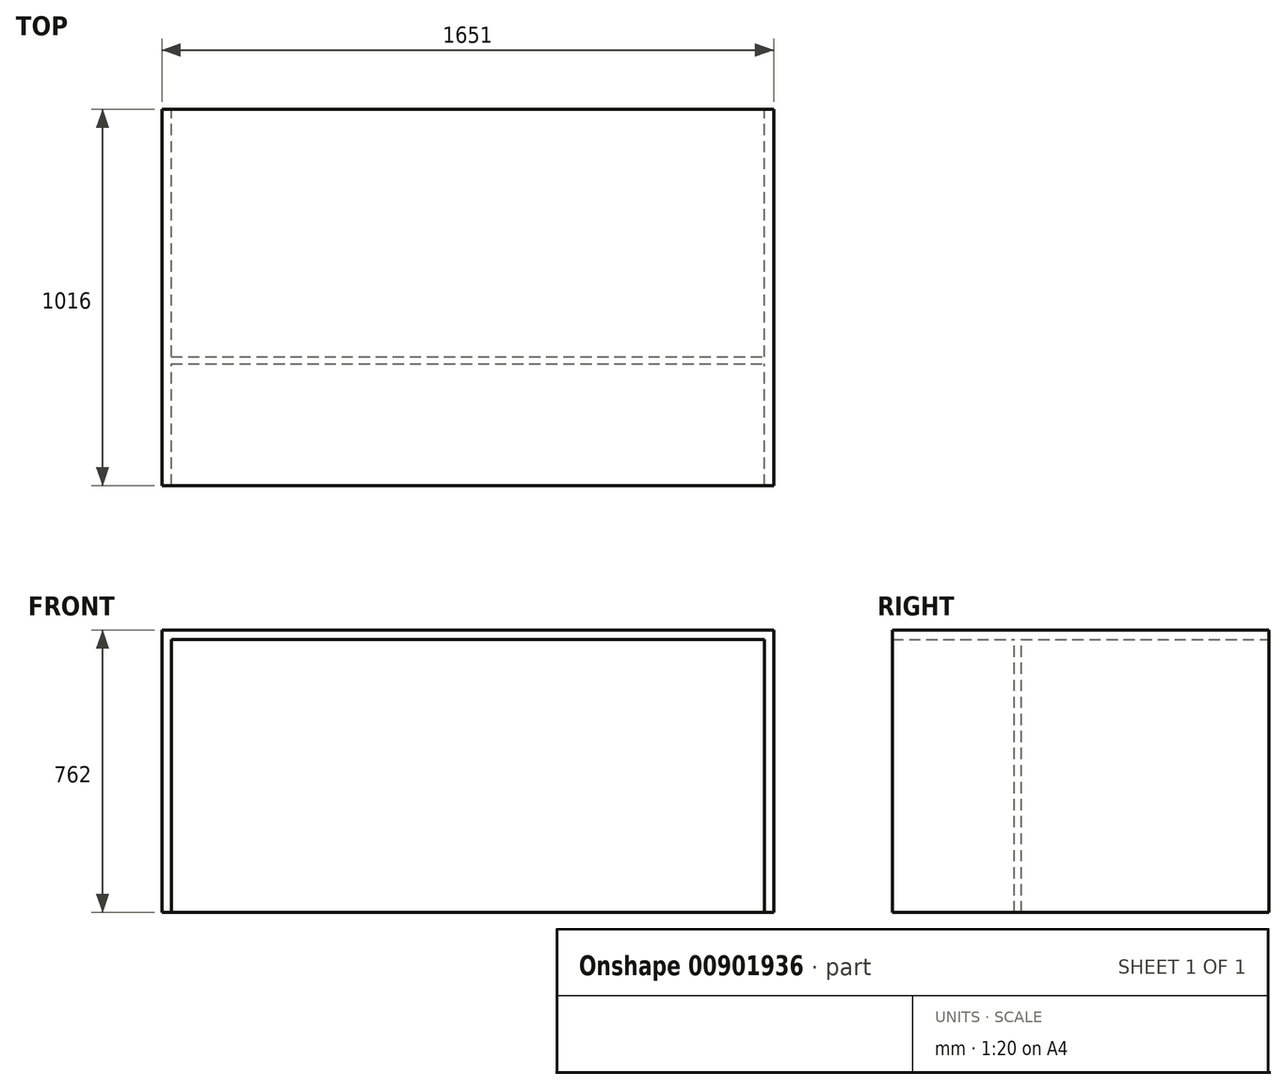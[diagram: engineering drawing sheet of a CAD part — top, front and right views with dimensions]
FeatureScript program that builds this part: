
annotation { "Feature Type Name" : "Feature", "Feature Type Description" : "" }
export const myFeature = defineFeature(function(context is Context, id is Id, definition is map)
    precondition{}
    {
        {
            assignVariable(context, id + "F0", {"name" : "height", "anyValue" : 762 * mm});
        }
        {
            assignVariable(context, id + "F1", {"name" : "width", "anyValue" : 1016 * mm});
        }
        {
            var Q0;
            Q0=qCreatedBy(makeId("Front.planeOp"),FACE);
            var sketch = newSketch(context, id + "F2", { "sketchPlane" : qUnion([Q0])});
            skLineSegment(sketch, "E0", {"start": v(0, 0) * mm, "end": v(25.4, 0) * mm});
            skLineSegment(sketch, "E1", {"start": v(25.4, 0) * mm, "end": v(25.4, 736.6) * mm});
            skLineSegment(sketch, "E2", {"start": v(25.4, 736.6) * mm, "end": v(0, 762) * mm});
            skLineSegment(sketch, "E3", {"start": v(0, 762) * mm, "end": v(0, 0) * mm});
            skLineSegment(sketch, "E4", {"start": v(0, 762) * mm, "end": v(1651, 762) * mm});
            skLineSegment(sketch, "E5", {"start": v(1651, 762) * mm, "end": v(1625.6, 736.6) * mm});
            skLineSegment(sketch, "E6", {"start": v(1625.6, 736.6) * mm, "end": v(25.4, 736.6) * mm});
            skLineSegment(sketch, "E7", {"start": v(1625.6, 736.6) * mm, "end": v(1625.6, 0) * mm});
            skLineSegment(sketch, "E8", {"start": v(1625.6, 0) * mm, "end": v(1651, 0) * mm});
            skLineSegment(sketch, "E9", {"start": v(1651, 0) * mm, "end": v(1651, 762) * mm});
            skSolve(sketch);
        }
        {
            var Q0;
            Q0=makeQuery(id+"F2.imprint","IMPRINT",FACE,{"disambiguationData":[TD([[makeQuery(id+"F2.imprint","IMPRINT",EDGE,{"derivedFrom":sQuery(id+"F2.wireOp",EDGE,"E0")}),1.0]])]});
            var Q1;
            Q1=makeQuery(id+"F2.imprint","IMPRINT",FACE,{"disambiguationData":[TD([[makeQuery(id+"F2.imprint","IMPRINT",EDGE,{"derivedFrom":sQuery(id+"F2.wireOp",EDGE,"E2")}),-1.0]])]});
            var Q2;
            Q2=makeQuery(id+"F2.imprint","IMPRINT",FACE,{"disambiguationData":[TD([[makeQuery(id+"F2.imprint","IMPRINT",EDGE,{"derivedFrom":sQuery(id+"F2.wireOp",EDGE,"E5")}),1.0]])]});
            extrude(context, id + "F3", {"entities" : qUnion([Q0, Q1, Q2]), "depth" : getVariable(context, 'width'), "offsetDistance" : 25.4 * mm});
        }
        {
            var Q0;
            Q0=makeQuery(id+"F3.opExtrude","SWEPT_FACE",FACE,{"disambiguationData":[OSD([sQuery(id+"F2.wireOp",EDGE,"E6")])]});
            var sketch = newSketch(context, id + "F4", { "sketchPlane" : qUnion([Q0])});
            skLineSegment(sketch, "E10", {"start": v(0, 677.33) * mm, "end": v(1651, 677.33) * mm, "construction": true});
            skLineSegment(sketch, "E11.bottom", {"start": v(9.53, 686.86) * mm, "end": v(1641.48, 686.86) * mm});
            skLineSegment(sketch, "E11.top", {"start": v(9.53, 667.8) * mm, "end": v(1641.48, 667.8) * mm});
            skLineSegment(sketch, "E11.left", {"start": v(9.53, 686.86) * mm, "end": v(9.53, 667.8) * mm});
            skLineSegment(sketch, "E11.right", {"start": v(1641.48, 686.86) * mm, "end": v(1641.48, 667.8) * mm});
            skSolve(sketch);
        }
        {
            var Q0;
            {var subQ0=sQuery(id+"F4.wireOp",EDGE,"E11.bottom");var subQ1=sQuery(id+"F2.wireOp",EDGE,"E6");var subQ2=makeQuery(id+"F3.opExtrude","SWEPT_EDGE",EDGE,{"disambiguationData":[OSD([sQuery(id+"F2.wireOp",EDGE,"E1"),sQuery(id+"F2.wireOp",EDGE,"E2"),subQ1])]});var subQ3=makeQuery(id+"F4.imprint","INTERSECT",VERTEX,{"derivedFrom":[subQ2,subQ0]});Q0=makeQuery(id+"F4.imprint","IMPRINT",FACE,{"disambiguationData":[TD([[makeQuery(id+"F4.imprint","IMPRINT",EDGE,{"disambiguationData":[TD([[subQ3,-1.0]])],"derivedFrom":subQ0}),-1.0]])]});}
            var Q1;
            Q1=makeQuery(id+"F3.opExtrude","SWEPT_FACE",FACE,{"disambiguationData":[OSD([sQuery(id+"F2.wireOp",EDGE,"E0")])]});
            extrude(context, id + "F5", {"entities" : qUnion([Q0]), "operationType" : NewBodyOperationType.ADD, "endBound" : BoundingType.UP_TO_SURFACE, "depth" : getVariable(context, 'height'), "endBoundEntityFace" : qUnion([Q1]), "offsetDistance" : 25.4 * mm});
        }
    });
